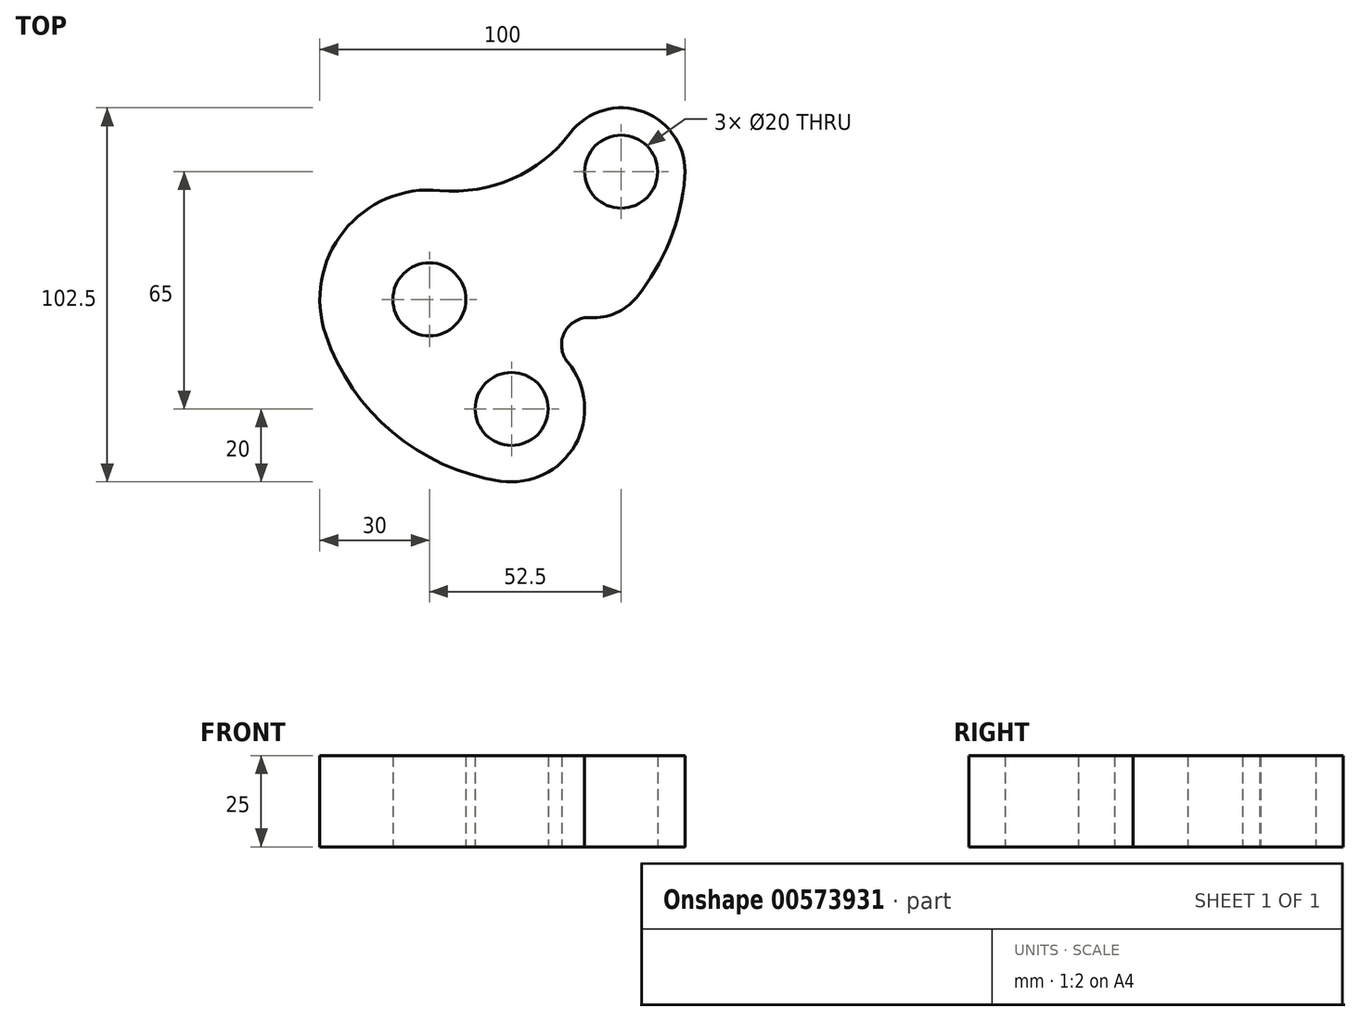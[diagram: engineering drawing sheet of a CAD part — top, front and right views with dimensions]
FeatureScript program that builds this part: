
annotation { "Feature Type Name" : "Feature", "Feature Type Description" : "" }
export const myFeature = defineFeature(function(context is Context, id is Id, definition is map)
    precondition{}
    {
        {
            var Q0;
            Q0=qCreatedBy(makeId("Top.planeOp"),FACE);
            var sketch = newSketch(context, id + "F0", { "sketchPlane" : qUnion([Q0])});
            skCircle(sketch, "E0", {"center": v(0, 0) * mm, "radius": 10 * mm});
            skArc(sketch, "E1", {"start": v(2.85, 29.86) * mm, "mid": v(-23.5, 18.65) * mm, "end": v(-28.44, -9.56) * mm});
            skCircle(sketch, "E2", {"center": v(52.5, 35) * mm, "radius": 10 * mm});
            skArc(sketch, "E3", {"start": v(69.94, 33.58) * mm, "mid": v(58.74, 51.35) * mm, "end": v(38.54, 45.56) * mm});
            skCircle(sketch, "E4", {"center": v(22.5, -30) * mm, "radius": 10 * mm});
            skArc(sketch, "E5", {"start": v(19.53, -49.78) * mm, "mid": v(39.91, -39.83) * mm, "end": v(37.9, -17.24) * mm});
            skArc(sketch, "E6", {"start": v(-28.44, -9.56) * mm, "mid": v(-10.11, -36.42) * mm, "end": v(19.53, -49.78) * mm});
            skArc(sketch, "E7", {"start": v(2.85, 29.86) * mm, "mid": v(22.74, 33.07) * mm, "end": v(38.54, 45.56) * mm});
            skArc(sketch, "E8", {"start": v(56.62, 0.51) * mm, "mid": v(51.03, -3.73) * mm, "end": v(44.12, -4.97) * mm});
            skArc(sketch, "E9", {"start": v(44.12, -4.97) * mm, "mid": v(37, -9.07) * mm, "end": v(37.9, -17.24) * mm});
            skArc(sketch, "E10", {"start": v(56.62, 0.51) * mm, "mid": v(65.8, 16.03) * mm, "end": v(69.94, 33.58) * mm});
            skSolve(sketch);
        }
        {
            var Q0;
            Q0 = qSketchRegion(id + "F0", true);
            extrude(context, id + "F1", {"entities" : qUnion([Q0]), "depth" : 25 * mm, "offsetDistance" : 25 * mm});
        }
    });
